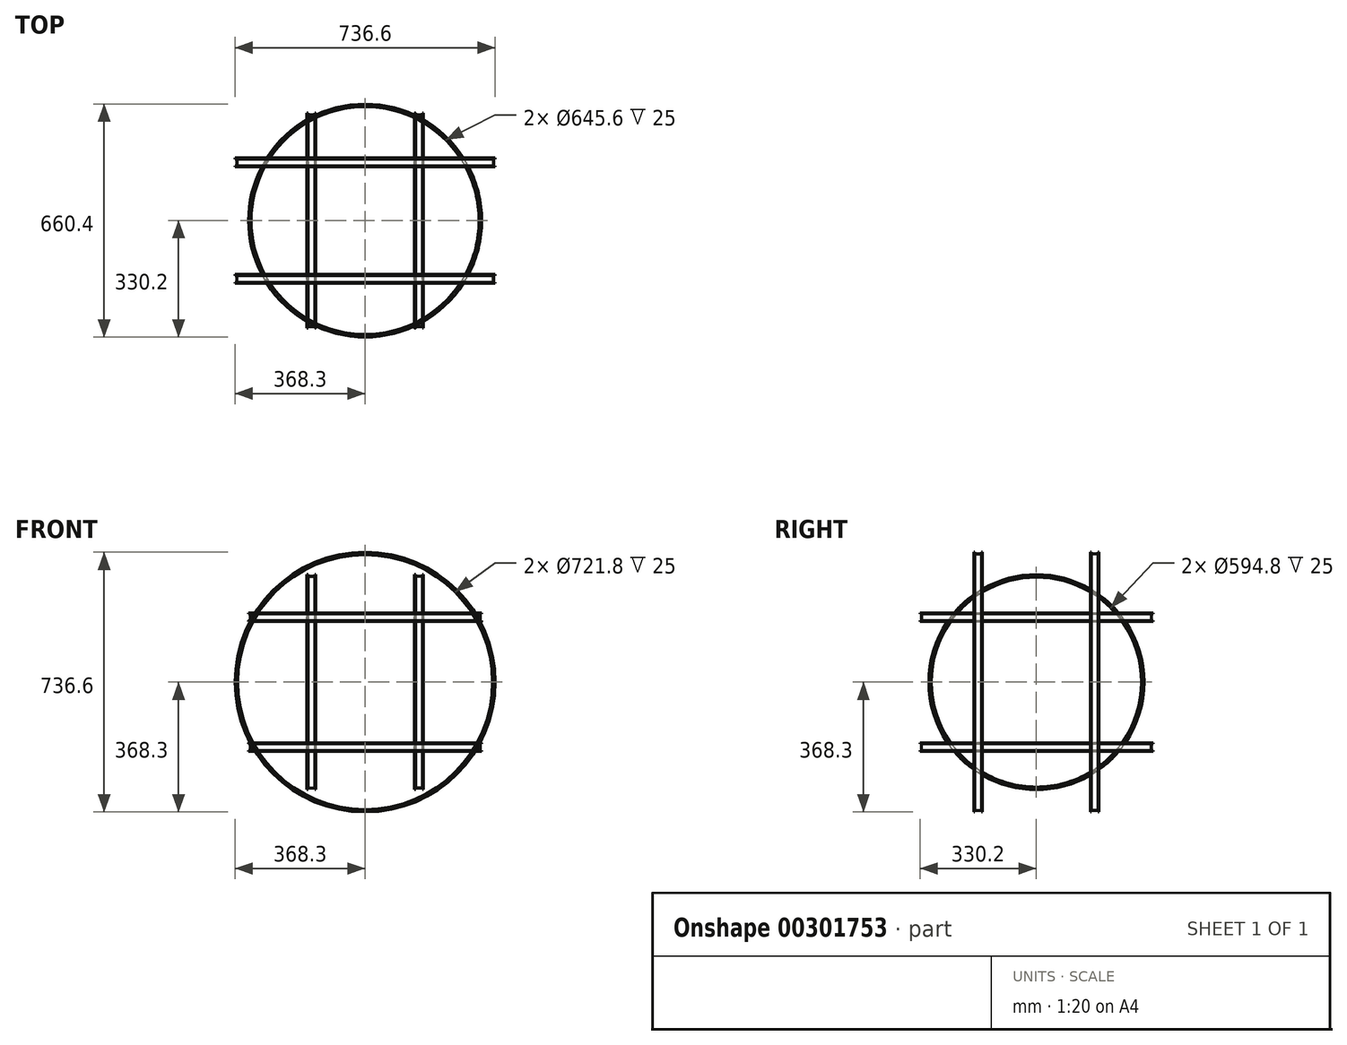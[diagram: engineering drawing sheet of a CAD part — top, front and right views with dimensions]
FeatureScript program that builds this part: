
annotation { "Feature Type Name" : "Feature", "Feature Type Description" : "" }
export const myFeature = defineFeature(function(context is Context, id is Id, definition is map)
    precondition{}
    {
        {
            assignVariable(context, id + "F0", {"name" : "Ld", "anyValue" : 736.6 * mm});
        }
        {
            assignVariable(context, id + "F1", {"name" : "Md", "anyValue" : 660.4 * mm});
        }
        {
            assignVariable(context, id + "F2", {"name" : "sd", "anyValue" : 609.6 * mm});
        }
        {
            assignVariable(context, id + "F3", {"name" : "Safstand", "anyValue" : 0.25 * getVariable(context, 'sd')});
        }
        {
            assignVariable(context, id + "F4", {"name" : "Mafstand", "anyValue" : 0.25 * getVariable(context, 'Md')});
        }
        {
            assignVariable(context, id + "F5", {"name" : "Lafstand", "anyValue" : 0.25 * getVariable(context, 'Ld')});
        }
        {
            assignVariable(context, id + "F6", {"name" : "Bredde", "anyValue" : 25});
        }
        {
            var Q0;
            Q0=qCreatedBy(makeId("Right.planeOp"),FACE);
            cPlane(context, id + "F7", {"entities" : qUnion([Q0]), "cplaneType" : CPlaneType.OFFSET, "offset" : (getVariable(context, 'Safstand')), "width" : 152.4 * mm, "height" : 152.4 * mm});
        }
        {
            var Q0;
            Q0=qCreatedBy(makeId("Front.planeOp"),FACE);
            cPlane(context, id + "F8", {"entities" : qUnion([Q0]), "cplaneType" : CPlaneType.OFFSET, "offset" : (getVariable(context, 'Mafstand')), "width" : 150 * mm, "height" : 150 * mm});
        }
        {
            var Q0;
            Q0=qCreatedBy(makeId("Top.planeOp"),FACE);
            cPlane(context, id + "F9", {"entities" : qUnion([Q0]), "cplaneType" : CPlaneType.OFFSET, "offset" : (getVariable(context, 'Lafstand')), "width" : 150 * mm, "height" : 150 * mm});
        }
        {
            var Q0;
            Q0=qCreatedBy(id+"F7.planeOp",FACE);
            var sketch = newSketch(context, id + "F10", { "sketchPlane" : qUnion([Q0])});
            skCircle(sketch, "E0", {"center": v(0, 0) * mm, "radius": 304.8 * mm});
            skCircle(sketch, "E1", {"center": v(0, 0) * mm, "radius": 297.4 * mm});
            skSolve(sketch);
        }
        {
            var Q0;
            Q0=qCreatedBy(id+"F9.planeOp",FACE);
            var sketch = newSketch(context, id + "F11", { "sketchPlane" : qUnion([Q0])});
            skCircle(sketch, "E2", {"center": v(0, 0) * mm, "radius": 322.8 * mm});
            skCircle(sketch, "E3", {"center": v(0, 0) * mm, "radius": 330.2 * mm});
            skSolve(sketch);
        }
        {
            var Q0;
            Q0=qCreatedBy(id+"F8.planeOp",FACE);
            var sketch = newSketch(context, id + "F12", { "sketchPlane" : qUnion([Q0])});
            skCircle(sketch, "E4", {"center": v(0, 0) * mm, "radius": 360.9 * mm});
            skCircle(sketch, "E5", {"center": v(0, 0) * mm, "radius": 368.3 * mm});
            skSolve(sketch);
        }
        {
            var Q0;
            Q0=makeQuery(id+"F12.imprint","IMPRINT",FACE,{"disambiguationData":[TD([[makeQuery(id+"F12.imprint","IMPRINT",EDGE,{"derivedFrom":sQuery(id+"F12.wireOp",EDGE,"E4")}),-1.0]])]});
            extrude(context, id + "F13", {"entities" : qUnion([Q0]), "depth" : (getVariable(context, 'Bredde')) / 2 * mm, "hasSecondDirection" : true, "secondDirectionOppositeDirection" : true, "secondDirectionDepth" : (getVariable(context, 'Bredde') / 2) * mm});
        }
        {
            var Q0;
            Q0=makeQuery(id+"F11.imprint","IMPRINT",FACE,{"disambiguationData":[TD([[makeQuery(id+"F11.imprint","IMPRINT",EDGE,{"derivedFrom":sQuery(id+"F11.wireOp",EDGE,"E2")}),-1.0]])]});
            extrude(context, id + "F14", {"entities" : qUnion([Q0]), "depth" : (getVariable(context, 'Bredde') / 2) * mm, "hasSecondDirection" : true, "secondDirectionOppositeDirection" : true, "secondDirectionDepth" : (getVariable(context, 'Bredde') / 2) * mm});
        }
        {
            var Q0;
            Q0=makeQuery(id+"F10.imprint","IMPRINT",FACE,{"disambiguationData":[TD([[makeQuery(id+"F10.imprint","IMPRINT",EDGE,{"derivedFrom":sQuery(id+"F10.wireOp",EDGE,"E0")}),1.0]])]});
            extrude(context, id + "F15", {"entities" : qUnion([Q0]), "depth" : (getVariable(context, 'Bredde') / 2) * mm, "hasSecondDirection" : true, "secondDirectionOppositeDirection" : true, "secondDirectionDepth" : (getVariable(context, 'Bredde') / 2) * mm});
        }
        {
            var Q0;
            Q0=makeQuery(id+"F14.opExtrude","SWEPT_BODY",BODY,{"disambiguationData":[OSD([sQuery(id+"F11.wireOp",EDGE,"E2"),sQuery(id+"F11.wireOp",EDGE,"E3")])]});
            var Q1;
            Q1=qCreatedBy(makeId("Top.planeOp"),FACE);
            mirror(context, id + "F16", {"entities" : qUnion([Q0]), "mirrorPlane" : qUnion([Q1])});
        }
        {
            var Q0;
            Q0=makeQuery(id+"F13.opExtrude","SWEPT_BODY",BODY,{"disambiguationData":[OSD([sQuery(id+"F12.wireOp",EDGE,"E4"),sQuery(id+"F12.wireOp",EDGE,"E5")])]});
            var Q1;
            Q1=qCreatedBy(makeId("Front.planeOp"),FACE);
            mirror(context, id + "F17", {"entities" : qUnion([Q0]), "mirrorPlane" : qUnion([Q1])});
        }
        {
            var Q0;
            Q0=makeQuery(id+"F15.opExtrude","SWEPT_BODY",BODY,{"disambiguationData":[OSD([sQuery(id+"F10.wireOp",EDGE,"E0"),sQuery(id+"F10.wireOp",EDGE,"E1")])]});
            var Q1;
            Q1=qCreatedBy(makeId("Right.planeOp"),FACE);
            mirror(context, id + "F18", {"entities" : qUnion([Q0]), "mirrorPlane" : qUnion([Q1])});
        }
        {
            var Q0;
            Q0=makeQuery(id+"F18.opPattern","COPY",FACE,{"derivedFrom":makeQuery(id+"F15.opExtrude","SWEPT_FACE",FACE,{"disambiguationData":[OSD([sQuery(id+"F10.wireOp",EDGE,"E0")])]}),"instanceName":"1"});
            var Q1;
            Q1=makeQuery(id+"F16.opPattern","COPY",FACE,{"derivedFrom":makeQuery(id+"F14.opExtrude","SWEPT_FACE",FACE,{"disambiguationData":[OSD([sQuery(id+"F11.wireOp",EDGE,"E3")])]}),"instanceName":"1"});
            var Q2;
            Q2=makeQuery(id+"F15.opExtrude","SWEPT_FACE",FACE,{"disambiguationData":[OSD([sQuery(id+"F10.wireOp",EDGE,"E0")])]});
            var Q3;
            Q3=makeQuery(id+"F14.opExtrude","SWEPT_FACE",FACE,{"disambiguationData":[OSD([sQuery(id+"F11.wireOp",EDGE,"E3")])]});
            var Q4;
            Q4=makeQuery(id+"F17.opPattern","COPY",FACE,{"derivedFrom":makeQuery(id+"F13.opExtrude","SWEPT_FACE",FACE,{"disambiguationData":[OSD([sQuery(id+"F12.wireOp",EDGE,"E5")])]}),"instanceName":"1"});
            var Q5;
            Q5=makeQuery(id+"F13.opExtrude","SWEPT_FACE",FACE,{"disambiguationData":[OSD([sQuery(id+"F12.wireOp",EDGE,"E5")])]});
            shell(context, id + "F19", {"entities" : qUnion([Q0, Q1, Q2, Q3, Q4, Q5]), "thickness" : 3 * mm});
        }
    });
